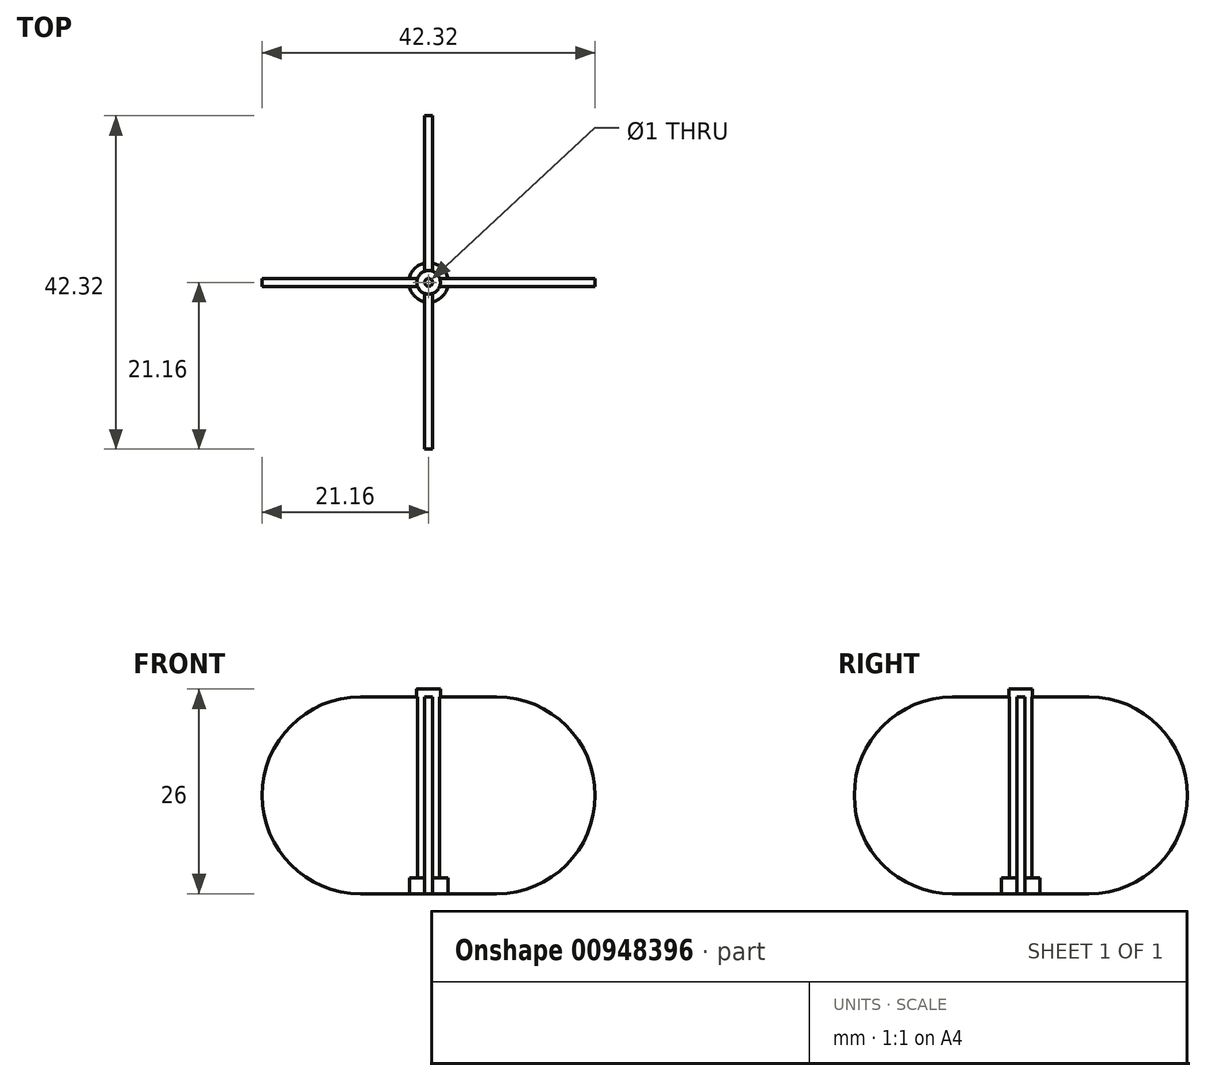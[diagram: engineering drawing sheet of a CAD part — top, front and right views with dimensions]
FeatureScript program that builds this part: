
annotation { "Feature Type Name" : "Feature", "Feature Type Description" : "" }
export const myFeature = defineFeature(function(context is Context, id is Id, definition is map)
    precondition{}
    {
        {
            var Q0;
            Q0=qCreatedBy(makeId("Top.planeOp"),FACE);
            var sketch = newSketch(context, id + "F0", { "sketchPlane" : qUnion([Q0])});
            skArc(sketch, "E0", {"start": v(-1.41, -0.5) * mm, "mid": v(-1.06, -1.06) * mm, "end": v(-0.5, -1.41) * mm});
            skCircle(sketch, "E1", {"center": v(0, 0) * mm, "radius": 0.5 * mm});
            skArc(sketch, "E2", {"start": v(-0.5, -8.66) * mm, "mid": v(0, -8.67) * mm, "end": v(0.5, -8.66) * mm});
            skLineSegment(sketch, "E3.bottom", {"start": v(-0.5, 8.66) * mm, "end": v(0.5, 8.66) * mm});
            skLineSegment(sketch, "E3.top", {"start": v(-0.5, -8.66) * mm, "end": v(0.5, -8.66) * mm});
            skLineSegment(sketch, "E3.left", {"start": v(-0.5, 8.66) * mm, "end": v(-0.5, 1.41) * mm});
            skLineSegment(sketch, "E3.right", {"start": v(0.5, 8.66) * mm, "end": v(0.5, 1.41) * mm});
            skLineSegment(sketch, "E4.bottom", {"start": v(8.66, 0.5) * mm, "end": v(1.41, 0.5) * mm});
            skLineSegment(sketch, "E4.top", {"start": v(8.66, -0.5) * mm, "end": v(1.41, -0.5) * mm});
            skLineSegment(sketch, "E4.left", {"start": v(8.66, 0.5) * mm, "end": v(8.66, -0.5) * mm});
            skLineSegment(sketch, "E4.right", {"start": v(-8.66, 0.5) * mm, "end": v(-8.66, -0.5) * mm});
            skArc(sketch, "E5.trimOffspring", {"start": v(8.66, -0.5) * mm, "mid": v(8.67, 0) * mm, "end": v(8.66, 0.5) * mm});
            skArc(sketch, "E6.trimOffspring", {"start": v(0.5, 8.66) * mm, "mid": v(0, 8.67) * mm, "end": v(-0.5, 8.66) * mm});
            skArc(sketch, "E7.trimOffspring", {"start": v(-8.66, 0.5) * mm, "mid": v(-8.67, 0) * mm, "end": v(-8.66, -0.5) * mm});
            skLineSegment(sketch, "E8.trimOffspring", {"start": v(-1.41, 0.5) * mm, "end": v(-8.66, 0.5) * mm});
            skLineSegment(sketch, "E9.trimOffspring", {"start": v(0.5, 0.5) * mm, "end": v(0, 0.5) * mm});
            skLineSegment(sketch, "E10.trimOffspring", {"start": v(0.5, -1.41) * mm, "end": v(0.5, -8.66) * mm});
            skLineSegment(sketch, "E11.trimOffspring", {"start": v(-0.5, -1.41) * mm, "end": v(-0.5, -8.66) * mm});
            skLineSegment(sketch, "E12.trimOffspring", {"start": v(-1.41, -0.5) * mm, "end": v(-8.66, -0.5) * mm});
            skArc(sketch, "E13.trimOffspring", {"start": v(-0.5, 1.41) * mm, "mid": v(-1.06, 1.06) * mm, "end": v(-1.41, 0.5) * mm});
            skArc(sketch, "E14.trimOffspring", {"start": v(1.41, 0.5) * mm, "mid": v(1.06, 1.06) * mm, "end": v(0.5, 1.41) * mm});
            skArc(sketch, "E15.trimOffspring", {"start": v(0.5, -1.41) * mm, "mid": v(1.06, -1.06) * mm, "end": v(1.41, -0.5) * mm});
            skSolve(sketch);
        }
        {
            var Q0;
            Q0=makeQuery(id+"F0.imprint","IMPRINT",FACE,{"disambiguationData":[TD([[makeQuery(id+"F0.imprint","IMPRINT",EDGE,{"derivedFrom":sQuery(id+"F0.wireOp",EDGE,"E0")}),1.0]])]});
            extrude(context, id + "F1", {"entities" : qUnion([Q0]), "depth" : 25 * mm, "offsetDistance" : 25 * mm});
        }
        {
            var Q0;
            Q0=makeQuery(id+"F1.opExtrude","CAP_FACE",FACE,{"disambiguationData":[OSD([sQuery(id+"F0.wireOp",EDGE,"E0"),sQuery(id+"F0.wireOp",EDGE,"E1"),sQuery(id+"F0.wireOp",EDGE,"E3.bottom"),sQuery(id+"F0.wireOp",EDGE,"E3.top"),sQuery(id+"F0.wireOp",EDGE,"E3.left"),sQuery(id+"F0.wireOp",EDGE,"E3.right"),sQuery(id+"F0.wireOp",EDGE,"E4.bottom"),sQuery(id+"F0.wireOp",EDGE,"E4.top"),sQuery(id+"F0.wireOp",EDGE,"E4.left"),sQuery(id+"F0.wireOp",EDGE,"E4.right"),sQuery(id+"F0.wireOp",EDGE,"E8.trimOffspring"),sQuery(id+"F0.wireOp",EDGE,"E10.trimOffspring"),sQuery(id+"F0.wireOp",EDGE,"E11.trimOffspring"),sQuery(id+"F0.wireOp",EDGE,"E12.trimOffspring"),sQuery(id+"F0.wireOp",EDGE,"E13.trimOffspring"),sQuery(id+"F0.wireOp",EDGE,"E14.trimOffspring"),sQuery(id+"F0.wireOp",EDGE,"E15.trimOffspring")])],"isStart":false});
            var sketch = newSketch(context, id + "F2", { "sketchPlane" : qUnion([Q0])});
            skCircle(sketch, "E16", {"center": v(0, 0) * mm, "radius": 1.5 * mm});
            skCircle(sketch, "E17", {"center": v(0, 0) * mm, "radius": 0.5 * mm});
            skSolve(sketch);
        }
        {
            var Q0;
            Q0=makeQuery(id+"F2.imprint","IMPRINT",FACE,{"disambiguationData":[TD([[makeQuery(id+"F2.imprint","IMPRINT",EDGE,{"derivedFrom":sQuery(id+"F2.wireOp",EDGE,"E17")}),-1.0]])]});
            extrude(context, id + "F3", {"entities" : qUnion([Q0]), "operationType" : NewBodyOperationType.ADD, "depth" : 1 * mm, "offsetDistance" : 25 * mm});
        }
        {
            var Q0;
            Q0=makeQuery(id+"F1.opExtrude","CAP_FACE",FACE,{"disambiguationData":[OSD([sQuery(id+"F0.wireOp",EDGE,"E0"),sQuery(id+"F0.wireOp",EDGE,"E1"),sQuery(id+"F0.wireOp",EDGE,"E3.bottom"),sQuery(id+"F0.wireOp",EDGE,"E3.top"),sQuery(id+"F0.wireOp",EDGE,"E3.left"),sQuery(id+"F0.wireOp",EDGE,"E3.right"),sQuery(id+"F0.wireOp",EDGE,"E4.bottom"),sQuery(id+"F0.wireOp",EDGE,"E4.top"),sQuery(id+"F0.wireOp",EDGE,"E4.left"),sQuery(id+"F0.wireOp",EDGE,"E4.right"),sQuery(id+"F0.wireOp",EDGE,"E8.trimOffspring"),sQuery(id+"F0.wireOp",EDGE,"E10.trimOffspring"),sQuery(id+"F0.wireOp",EDGE,"E11.trimOffspring"),sQuery(id+"F0.wireOp",EDGE,"E12.trimOffspring"),sQuery(id+"F0.wireOp",EDGE,"E13.trimOffspring"),sQuery(id+"F0.wireOp",EDGE,"E14.trimOffspring"),sQuery(id+"F0.wireOp",EDGE,"E15.trimOffspring")])],"isStart":true});
            var sketch = newSketch(context, id + "F4", { "sketchPlane" : qUnion([Q0])});
            skCircle(sketch, "E18", {"center": v(0, 0) * mm, "radius": 2.5 * mm});
            skCircle(sketch, "E19", {"center": v(0, 0) * mm, "radius": 0.5 * mm});
            skSolve(sketch);
        }
        {
            var Q0;
            Q0 = qSketchRegion(id + "F4", true);
            extrude(context, id + "F5", {"entities" : qUnion([Q0]), "operationType" : NewBodyOperationType.ADD, "oppositeDirection" : true, "depth" : 2 * mm, "offsetDistance" : 25 * mm});
        }
        {
            var Q0;
            Q0=makeQuery(id+"F1.opExtrude","SWEPT_FACE",FACE,{"disambiguationData":[OSD([sQuery(id+"F0.wireOp",EDGE,"E10.trimOffspring")])]});
            var sketch = newSketch(context, id + "F6", { "sketchPlane" : qUnion([Q0])});
            skArc(sketch, "E20", {"start": v(-8.66, 25) * mm, "mid": v(-21.16, 12.5) * mm, "end": v(-8.66, 0) * mm});
            skSolve(sketch);
        }
        {
            var Q0;
            Q0=makeQuery(id+"F6.imprint","IMPRINT",FACE,{"disambiguationData":[TD([[makeQuery(id+"F6.imprint","IMPRINT",EDGE,{"derivedFrom":sQuery(id+"F6.wireOp",EDGE,"E20")}),1.0]])]});
            extrude(context, id + "F7", {"entities" : qUnion([Q0]), "operationType" : NewBodyOperationType.ADD, "oppositeDirection" : true, "depth" : 1 * mm, "offsetDistance" : 25 * mm});
        }
        {
            var Q0;
            Q0=makeQuery(id+"F1.opExtrude","SWEPT_FACE",FACE,{"disambiguationData":[OSD([sQuery(id+"F0.wireOp",EDGE,"E8.trimOffspring")])]});
            var sketch = newSketch(context, id + "F8", { "sketchPlane" : qUnion([Q0])});
            skArc(sketch, "E21", {"start": v(8.66, 0) * mm, "mid": v(21.16, 12.5) * mm, "end": v(8.66, 25) * mm});
            skSolve(sketch);
        }
        {
            var Q0;
            Q0 = qSketchRegion(id + "F8", true);
            var Q1;
            Q1=makeQuery(id+"F8.imprint","IMPRINT",FACE,{"disambiguationData":[TD([[makeQuery(id+"F8.imprint","IMPRINT",EDGE,{"derivedFrom":sQuery(id+"F8.wireOp",EDGE,"E21")}),1.0]])]});
            extrude(context, id + "F9", {"entities" : qUnion([Q0, Q1]), "operationType" : NewBodyOperationType.ADD, "oppositeDirection" : true, "depth" : 1 * mm, "offsetDistance" : 25 * mm});
        }
        {
            var Q0;
            Q0=makeQuery(id+"F1.opExtrude","SWEPT_FACE",FACE,{"disambiguationData":[OSD([sQuery(id+"F0.wireOp",EDGE,"E3.left")])]});
            var sketch = newSketch(context, id + "F10", { "sketchPlane" : qUnion([Q0])});
            skArc(sketch, "E22", {"start": v(-8.66, 25) * mm, "mid": v(-21.16, 12.5) * mm, "end": v(-8.66, 0) * mm});
            skSolve(sketch);
        }
        {
            var Q0;
            Q0 = qSketchRegion(id + "F10", true);
            var Q1;
            Q1=makeQuery(id+"F10.imprint","IMPRINT",FACE,{"disambiguationData":[TD([[makeQuery(id+"F10.imprint","IMPRINT",EDGE,{"derivedFrom":sQuery(id+"F10.wireOp",EDGE,"E22")}),1.0]])]});
            extrude(context, id + "F11", {"entities" : qUnion([Q0, Q1]), "operationType" : NewBodyOperationType.ADD, "oppositeDirection" : true, "depth" : 1 * mm, "offsetDistance" : 25 * mm});
        }
        {
            var Q0;
            Q0=makeQuery(id+"FxQR0UVdZLE1twP_1.opExtrude","CAP_FACE",FACE,{"disambiguationData":[OSD([sQuery(id+"F0.wireOp",EDGE,"E4.bottom"),sQuery(id+"F0.wireOp",EDGE,"E4.left"),sQuery(id+"F0.wireOp",EDGE,"E5.trimOffspring"),sQuery(id+"FRQ2x6zC5XSGJ2S_1.wireOp",EDGE,"wuJA3gd2-V3mD-4evz-5n8I-o2N4So9OkdGB")])],"isStart":true});
            var Q1;
            Q1=makeQuery(id+"F1.opExtrude","SWEPT_FACE",FACE,{"disambiguationData":[OSD([sQuery(id+"F0.wireOp",EDGE,"E4.bottom")])]});
            extrude(context, id + "F12", {"entities" : qUnion([Q0, Q1]), "oppositeDirection" : true, "depth" : 1 * mm, "offsetDistance" : 25 * mm});
        }
        {
            var Q0;
            Q0=makeQuery(id+"F1.opExtrude","SWEPT_FACE",FACE,{"disambiguationData":[OSD([sQuery(id+"F0.wireOp",EDGE,"E4.bottom")])]});
            var sketch = newSketch(context, id + "F13", { "sketchPlane" : qUnion([Q0])});
            skArc(sketch, "E23", {"start": v(-8.66, 25) * mm, "mid": v(-21.16, 12.5) * mm, "end": v(-8.66, 0) * mm});
            skSolve(sketch);
        }
        {
            var Q0;
            Q0 = qSketchRegion(id + "F13", true);
            var Q1;
            Q1=makeQuery(id+"F13.imprint","IMPRINT",FACE,{"disambiguationData":[TD([[makeQuery(id+"F13.imprint","IMPRINT",EDGE,{"derivedFrom":sQuery(id+"F13.wireOp",EDGE,"E23")}),1.0]])]});
            extrude(context, id + "F14", {"entities" : qUnion([Q0, Q1]), "operationType" : NewBodyOperationType.ADD, "oppositeDirection" : true, "depth" : 1 * mm, "offsetDistance" : 25 * mm});
        }
    });
